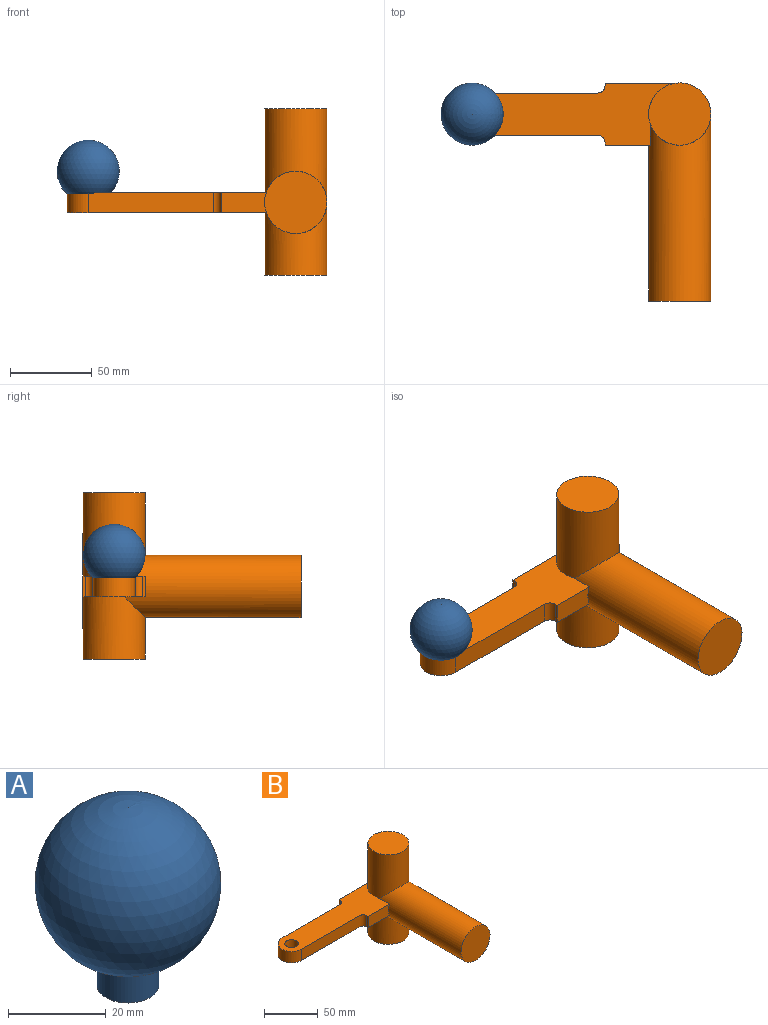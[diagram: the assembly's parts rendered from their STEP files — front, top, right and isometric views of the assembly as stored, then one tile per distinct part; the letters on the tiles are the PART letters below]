
ASSEMBLY  parts=2 mates=1
PART A: 3 faces, bbox 38.1x38.1x44.5 mm
  f0: cylinder r=6.35mm len=12.7mm, axis (0,0,1), area 296.8mm2, adj f1,f2
  f1: plane 12.7x12.7mm, normal (0,0,-1), area 126.7mm2, adj f0
  f2: sphere r=19.05mm, area 4430mm2, adj f0
PART B: 17 faces, bbox 158.8x133.4x101.6 mm
  f0: plane 45.72x12.7mm, normal (0,1,0), area 580.6mm2, adj f2,f3,f8,f9
  f1: plane 27.76x12.7mm, normal (0,-1,0), area 343.3mm2, adj f2,f4,f8,f10
  f2: plane 139.7x38.1mm, normal (0,0,1), area 3330.9mm2, adj f0,f1,f3,f4,f9,f10,f11,f12
  f3: cylinder r=19.05mm len=101.6mm, axis (0,0,-1), area 10288.6mm2, adj f0,f2,f4,f5,f6,f8
  f4: cylinder r=19.05mm len=114.3mm, axis (0,1,0), area 12024.3mm2, adj f1,f2,f3,f7,f8
  f5: plane 38.1x38.1mm, normal (0,0,1), area 1140.1mm2, adj f3
  f6: plane 38.1x38.1mm, normal (0,0,-1), area 1140.1mm2, adj f3
  f7: plane 38.1x38.1mm, normal (0,-1,0), area 1140.1mm2, adj f4
  f8: plane 139.7x38.1mm, normal (0,0,-1), area 3330.9mm2, adj f0,f1,f3,f4,f9,f10,f11,f12
  f9: plane 12.7x1.54mm, normal (-1,0,0), area 19.5mm2, adj f0,f2,f8,f16
  f10: plane 12.7x1.54mm, normal (-1,0,0), area 19.5mm2, adj f1,f2,f8,f15
  f11: plane 76.72x12.7mm, normal (0,1,0), area 974.4mm2, adj f2,f8,f13,f16
  f12: plane 76.72x12.7mm, normal (0,-1,0), area 974.4mm2, adj f2,f8,f13,f15
  f13: cylinder r=12.7mm len=25.4mm, axis (0,0,1), area 506.7mm2, adj f2,f8,f11,f12
  f14: cylinder r=6.35mm len=12.7mm, axis (0,0,1), area 506.7mm2, adj f2,f8
  f15: cylinder r=4.57mm len=12.7mm, axis (0,0,-1), area 91mm2, adj f2,f8,f10,f12
  f16: cylinder r=4.57mm len=12.7mm, axis (0,0,-1), area 91mm2, adj f2,f8,f9,f11
PLACE A t=(-127,0,-38.1)mm
PLACE B t=(0,0,-101.6)mm
MATE fastened A.f0 <-> B.f14  axis (0,0,-1) through (-127,0,-63.5)mm
